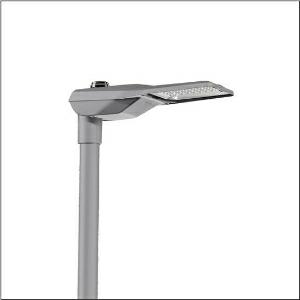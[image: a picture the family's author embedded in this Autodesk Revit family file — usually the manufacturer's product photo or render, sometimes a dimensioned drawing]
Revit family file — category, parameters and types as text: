
# Revit family: streetlight_sl_21_mini___pl52_5xe6h37n08gb_6e65
name_source: partatom
category: Lighting Fixtures
units: mm (PartAtom-declared; Revit-internal decimal feet)

## family parameters
Cut with Voids When Loaded = No
Host = Face
Light Source = No
Part Type = Normal
Room Calculation Point = No
Round Connector Dimension = Use Diameter
Shared = No

## types (1)
- --- (1 x LED, 5840 lm, 40.4 W, 3000K)
    Apparent Load = 40 VA
    CIE Flux Codes = 27 59 98 100 100
    Color Rendering = 70
    Color Temperature = 3000K
    Default Elevation = 1800 mm
    Description = Streetlight SL 21 mini, mast luminaire, primary light control with lens, of PMMA, primary optical cover: cover, of toughened safety glass, transparent, light distribution: PL52, light emission: direct distribution, primary light characteristic: asymmetric, installation type: side-entry, LED, 3G 1.5mm², High Power LED, rated luminous flux: 5.840lm, luminous efficacy: 145lm/W, light colour: 730, colour temperature: 3000K, control gear: NEMA (7pin), control: overheat protection, pre-setting: linear dimming characteristic, constant luminous flux control, time-dependent luminous flux control, flexible luminous flux parameterisation, mains connection: 230..240V, AC, 50/60Hz, connection cable pre-assembled, cable length: 8,5m, wiring characteristics: H07RN-F, start of lifetime: 40W, end of service life: 41W, reduction: 19W, luminaire housing, of diecast aluminium (EN AC-44300), powder-coated, SITECO metallic grey (DB 702S), corrosivity category C5 high according to DIN EN ISO 12944, multi-level sealing system, sealing non-destructively replaceable, inclination adjustable: 0°, 5°, 10°, 15°, length: 628mm, width: 235mm, height: 110mm, spigot size: 42mm (side-entry), mounting height: 4..8m, protection rating (complete): IP66, insulation class (complete): insulation class I (protective earthing), certification: CE, ENEC, ENEC+, VDE, impact resistance: IK10, permissible operating ambient temperature for outdoor applications: -40..+50°C, standard-compliant lighting for roads and squares, packaging unit: 1 piece

Light Distribution: PL52
    Height = 110 mm
    Lamp = 1 x LED
    Lamp Light Flux = 5840 lm
    Lamp Power = 40.4 W
    Lamp count = 1
    Length = 625 mm
    Luminous efficacy = 145 lm/W
    Manufacturer = Siteco
    ModVariant = No
    Model = 5XE6H37N08GB
    Number of Poles = 1
    OnlyDefault = Yes
    Power Factor = 1
    Product Name = Streetlight SL 21 mini | PL52
    Product group = mast luminaire | pylon top
    ProductGroupID = 6100
    Protection Class = Protection class I
    Protection Degree = IP 66
    RLX_Detail_Level = 1
    RLX_Emergency_Light_Flux = 0 lm
    RLX_Emergency_Type = 0
    RLX_Emergency_Type_DB = No
    RlxData = <blob elided: 35477 chars, md5=13f7e2c3>
    Socket = socket
    Standby Power = 0 W
    System Light Flux = 5840 lm
    System Power = 40 W
    Type Comments = factory setting: luminous flux: 100 % | dim-lin: 254 | 812 mA
    Type Image = l_1294379.jpg
    URL = http://relux.com
    VarID = @adj_136579
    Voltage = 0 V
    Weight = 0.00 kg
    Width = 234 mm

## geometry (parser evidence)
native form markers: Blend x4, Sweep x11
no freeform markers — native parametric forms only
